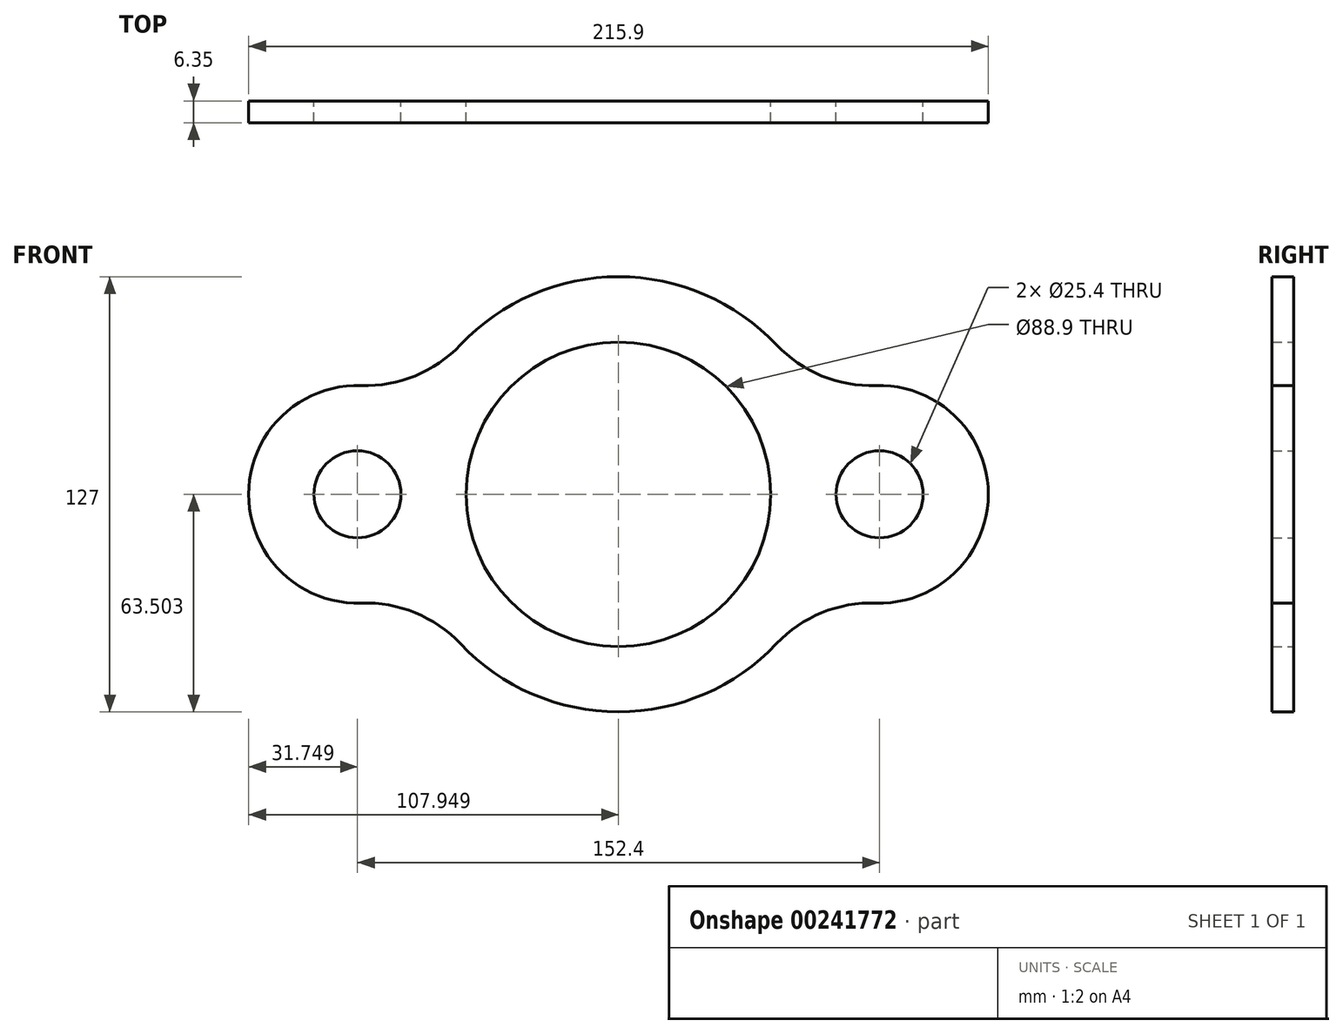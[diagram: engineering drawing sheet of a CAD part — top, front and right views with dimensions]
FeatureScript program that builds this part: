
annotation { "Feature Type Name" : "Feature", "Feature Type Description" : "" }
export const myFeature = defineFeature(function(context is Context, id is Id, definition is map)
    precondition{}
    {
        {
            var Q0;
            Q0=qCreatedBy(makeId("Front.planeOp"),FACE);
            var sketch = newSketch(context, id + "F0", { "sketchPlane" : qUnion([Q0])});
            skLineSegment(sketch, "E0", {"start": v(85.34, 9.75) * mm, "end": v(-67.06, 9.75) * mm, "construction": true});
            skCircle(sketch, "E1", {"center": v(-67.06, 9.75) * mm, "radius": 12.7 * mm});
            skCircle(sketch, "E2", {"center": v(85.34, 9.75) * mm, "radius": 12.7 * mm});
            skCircle(sketch, "E3", {"center": v(9.14, 9.75) * mm, "radius": 44.45 * mm});
            skArc(sketch, "E4", {"start": v(84.26, -21.98) * mm, "mid": v(117.09, 9.75) * mm, "end": v(84.26, 41.48) * mm});
            skArc(sketch, "E5", {"start": v(-65.98, 41.48) * mm, "mid": v(-98.81, 9.75) * mm, "end": v(-65.98, -21.98) * mm});
            skArc(sketch, "E6", {"start": v(-37, -33.88) * mm, "mid": v(9.14, -53.75) * mm, "end": v(55.28, -33.88) * mm});
            skArc(sketch, "E7.trimOffspring", {"start": v(55.28, 53.38) * mm, "mid": v(9.14, 73.25) * mm, "end": v(-37, 53.38) * mm});
            skArc(sketch, "E8.filletArc", {"start": v(-65.98, 41.48) * mm, "mid": v(-50.2, 44.32) * mm, "end": v(-37, 53.38) * mm});
            skArc(sketch, "E9.filletArc", {"start": v(55.28, 53.38) * mm, "mid": v(68.49, 44.32) * mm, "end": v(84.26, 41.48) * mm});
            skArc(sketch, "E10.filletArc", {"start": v(84.26, -21.98) * mm, "mid": v(68.49, -24.81) * mm, "end": v(55.28, -33.88) * mm});
            skArc(sketch, "E11.filletArc", {"start": v(-37, -33.88) * mm, "mid": v(-50.2, -24.81) * mm, "end": v(-65.98, -21.98) * mm});
            skSolve(sketch);
        }
        {
            var Q0;
            Q0=makeQuery(id+"F0.imprint","IMPRINT",FACE,{"disambiguationData":[TD([[makeQuery(id+"F0.imprint","IMPRINT",EDGE,{"derivedFrom":sQuery(id+"F0.wireOp",EDGE,"E1")}),-1.0]])]});
            extrude(context, id + "F1", {"entities" : qUnion([Q0]), "depth" : 6.35 * mm});
        }
    });
